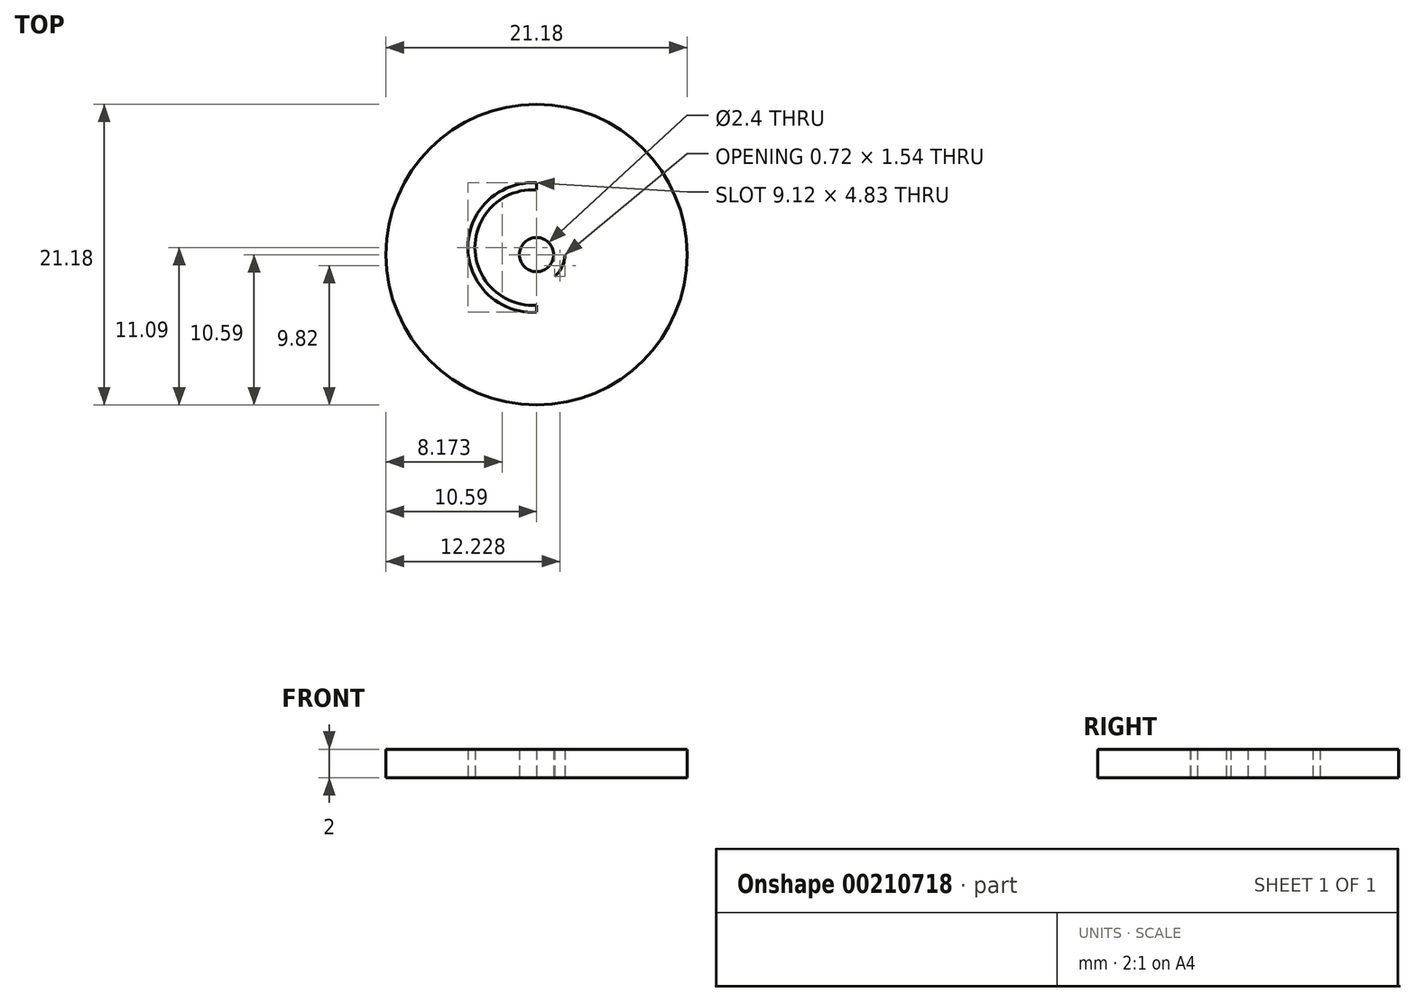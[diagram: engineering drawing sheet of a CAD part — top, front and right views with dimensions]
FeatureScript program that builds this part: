
annotation { "Feature Type Name" : "Feature", "Feature Type Description" : "" }
export const myFeature = defineFeature(function(context is Context, id is Id, definition is map)
    precondition{}
    {
        {
            var Q0;
            Q0=qCreatedBy(makeId("Top.planeOp"),FACE);
            var sketch = newSketch(context, id + "F0", { "sketchPlane" : qUnion([Q0])});
            skPoint(sketch, "E0", {"position": v(-1.84, 3.56) * mm});
            skArc(sketch, "E1", {"start": v(0, -3.56) * mm, "mid": v(3.33, 0) * mm, "end": v(0, 3.56) * mm});
            skArc(sketch, "E2", {"start": v(0, 3.56) * mm, "mid": v(-3.27, 0.5) * mm, "end": v(0, -2.56) * mm});
            skArc(sketch, "E3", {"start": v(0, -2.56) * mm, "mid": v(2.4, 0) * mm, "end": v(0, 2.56) * mm});
            skArc(sketch, "E4", {"start": v(0, 2.56) * mm, "mid": v(-2.2, 0.5) * mm, "end": v(0, -1.56) * mm});
            skPoint(sketch, "E5.end.orphan", {"position": v(-0.75, 4.56) * mm});
            skPoint(sketch, "E6.orphan", {"position": v(4, -0.14) * mm});
            skPoint(sketch, "E7.center.orphan", {"position": v(0, 0) * mm});
            skArc(sketch, "E8", {"start": v(0, -3.56) * mm, "mid": v(-4.33, 0.5) * mm, "end": v(0, 4.56) * mm});
            skLineSegment(sketch, "E9", {"start": v(0, 2.56) * mm, "end": v(0, 3.06) * mm});
            skLineSegment(sketch, "E10", {"start": v(0, -2.56) * mm, "end": v(0, -3.06) * mm});
            skLineSegment(sketch, "E11", {"start": v(0, 3.56) * mm, "end": v(0, 4.06) * mm});
            skLineSegment(sketch, "E12", {"start": v(0, -3.56) * mm, "end": v(0, -4.06) * mm});
            skLineSegment(sketch, "E13", {"start": v(0, 4.56) * mm, "end": v(0, 5.06) * mm});
            skArc(sketch, "E14", {"start": v(0, 3.06) * mm, "mid": v(-2.7, 0.5) * mm, "end": v(0, -2.06) * mm});
            skPoint(sketch, "E15", {"position": v(-2.2, 0.66) * mm});
            skPoint(sketch, "E16", {"position": v(-2.68, 0.78) * mm});
            skArc(sketch, "E17", {"start": v(0, -3.06) * mm, "mid": v(2.9, 0) * mm, "end": v(0, 3.06) * mm});
            skPoint(sketch, "E18", {"position": v(2.4, 0) * mm});
            skPoint(sketch, "E19", {"position": v(2.9, 0) * mm});
            skPoint(sketch, "E19.positionSnap0", {"position": v(2.9, 0) * mm});
            skArc(sketch, "E20", {"start": v(0, 4.06) * mm, "mid": v(-3.77, 0.5) * mm, "end": v(0, -3.06) * mm});
            skPoint(sketch, "E21", {"position": v(-3.77, 0.5) * mm});
            skPoint(sketch, "E22", {"position": v(-3.27, 0.5) * mm});
            skArc(sketch, "E23", {"start": v(0, -4.06) * mm, "mid": v(3.83, 0) * mm, "end": v(0, 4.06) * mm});
            skPoint(sketch, "E24", {"position": v(3.33, 0) * mm});
            skPoint(sketch, "E25", {"position": v(3.83, 0) * mm});
            skPoint(sketch, "E25.positionSnap0", {"position": v(3.83, 0) * mm});
            skArc(sketch, "E26", {"start": v(0, 5.06) * mm, "mid": v(-4.83, 0.5) * mm, "end": v(0, -4.06) * mm});
            skPoint(sketch, "E27", {"position": v(-4.33, 0.5) * mm});
            skPoint(sketch, "E28", {"position": v(-4.83, 0.5) * mm});
            skPoint(sketch, "E29", {"position": v(0, -4.56) * mm});
            skLineSegment(sketch, "E30", {"start": v(0, -4.56) * mm, "end": v(0, -5.06) * mm});
            skPoint(sketch, "E31", {"position": v(0, -5.56) * mm});
            skLineSegment(sketch, "E32", {"start": v(0, -5.56) * mm, "end": v(0, -6.06) * mm});
            skPoint(sketch, "E33", {"position": v(0, -6.56) * mm});
            skLineSegment(sketch, "E34", {"start": v(0, -6.56) * mm, "end": v(0, -7.06) * mm});
            skLineSegment(sketch, "E35", {"start": v(4.33, 0) * mm, "end": v(4.83, 0) * mm});
            skLineSegment(sketch, "E36", {"start": v(5.33, 0) * mm, "end": v(5.83, 0) * mm});
            skLineSegment(sketch, "E37", {"start": v(6.33, 0) * mm, "end": v(6.88, 0) * mm});
            skArc(sketch, "E38", {"start": v(0, -4.56) * mm, "mid": v(3.07, -3.14) * mm, "end": v(4.33, 0) * mm});
            skArc(sketch, "E39", {"start": v(0, -5.06) * mm, "mid": v(3.43, -3.5) * mm, "end": v(4.83, 0) * mm});
            skArc(sketch, "E40", {"start": v(4.33, 0) * mm, "mid": v(3.07, 3.14) * mm, "end": v(0, 4.56) * mm});
            skPoint(sketch, "E41", {"position": v(-2.7, 0.5) * mm});
            skPoint(sketch, "E42", {"position": v(-2.2, 0.5) * mm});
            skPoint(sketch, "E42.positionSnap0", {"position": v(-2.2, 0.5) * mm});
            skArc(sketch, "E43", {"start": v(4.83, 0) * mm, "mid": v(3.43, 3.5) * mm, "end": v(0, 5.06) * mm});
            skLineSegment(sketch, "E44", {"start": v(0, 5.56) * mm, "end": v(0, 6.06) * mm});
            skLineSegment(sketch, "E45", {"start": v(0, 6.56) * mm, "end": v(0, 7.06) * mm});
            skLineSegment(sketch, "E46", {"start": v(0, 7.56) * mm, "end": v(0, 8.06) * mm});
            skArc(sketch, "E47", {"start": v(5.33, 0) * mm, "mid": v(3.83, 3.9) * mm, "end": v(0, 5.56) * mm});
            skArc(sketch, "E48", {"start": v(0, 5.56) * mm, "mid": v(-5.33, 0.5) * mm, "end": v(0, -4.56) * mm});
            skArc(sketch, "E49", {"start": v(0, 6.06) * mm, "mid": v(-5.83, 0.5) * mm, "end": v(0, -5.06) * mm});
            skArc(sketch, "E50", {"start": v(0, -5.56) * mm, "mid": v(3.78, -3.85) * mm, "end": v(5.33, 0) * mm});
            skArc(sketch, "E51", {"start": v(0, -6.06) * mm, "mid": v(5.83, 0) * mm, "end": v(0, 6.06) * mm});
            skArc(sketch, "E52", {"start": v(0, 6.56) * mm, "mid": v(-6.3, 0.5) * mm, "end": v(0, -5.56) * mm});
            skArc(sketch, "E53", {"start": v(0, 7.06) * mm, "mid": v(-6.8, 0.5) * mm, "end": v(0, -6.06) * mm});
            skPoint(sketch, "E54", {"position": v(-6.8, 0.5) * mm});
            skPoint(sketch, "E55", {"position": v(-6.3, 0.5) * mm});
            skPoint(sketch, "E56", {"position": v(-5.83, 0.5) * mm});
            skPoint(sketch, "E57", {"position": v(-5.33, 0.5) * mm});
            skArc(sketch, "E58", {"start": v(0, -6.56) * mm, "mid": v(6.33, 0) * mm, "end": v(0, 6.56) * mm});
            skArc(sketch, "E59", {"start": v(0, -7.06) * mm, "mid": v(6.88, 0) * mm, "end": v(0, 7.06) * mm});
            skArc(sketch, "E60", {"start": v(0, 7.56) * mm, "mid": v(-7.3, 0.5) * mm, "end": v(0, -6.56) * mm});
            skArc(sketch, "E61", {"start": v(0, 8.06) * mm, "mid": v(-7.8, 0.5) * mm, "end": v(0, -7.06) * mm});
            skArc(sketch, "E62", {"start": v(1.28, -1.54) * mm, "mid": v(0.61, 1.9) * mm, "end": v(-1.93, -0.5) * mm});
            skLineSegment(sketch, "E63", {"start": v(0, 0) * mm, "end": v(1.67, -1.1) * mm});
            skArc(sketch, "E64", {"start": v(0, -2.06) * mm, "mid": v(1.4, -1.42) * mm, "end": v(2, 0) * mm});
            skCircle(sketch, "E65", {"center": v(0, 0) * mm, "radius": 1.2 * mm});
            skPoint(sketch, "E66", {"position": v(1, -0.67) * mm});
            skPoint(sketch, "E67", {"position": v(-1.93, -0.5) * mm});
            skCircle(sketch, "E68", {"center": v(0, 0) * mm, "radius": 8.6 * mm});
            skCircle(sketch, "E69", {"center": v(0, 0) * mm, "radius": 10.6 * mm});
            skArc(sketch, "E70", {"start": v(0, 8.06) * mm, "mid": v(0.58, 8.13) * mm, "end": v(1, 8.54) * mm});
            skArc(sketch, "E71", {"start": v(0, 7.56) * mm, "mid": v(1.07, 7.74) * mm, "end": v(1.94, 8.37) * mm});
            skSolve(sketch);
        }
        {
            var Q0;
            Q0=makeQuery(id+"F0.imprint","IMPRINT",FACE,{"disambiguationData":[TD([[makeQuery(id+"F0.imprint","IMPRINT",EDGE,{"derivedFrom":sQuery(id+"F0.wireOp",EDGE,"E69")}),1.0]])]});
            var Q1;
            Q1=makeQuery(id+"F0.imprint","IMPRINT",FACE,{"disambiguationData":[TD([[makeQuery(id+"F0.imprint","IMPRINT",EDGE,{"derivedFrom":sQuery(id+"F0.wireOp",EDGE,"E46")}),-1.0]])]});
            var Q2;
            Q2=makeQuery(id+"F0.imprint","IMPRINT",FACE,{"disambiguationData":[TD([[makeQuery(id+"F0.imprint","IMPRINT",EDGE,{"derivedFrom":sQuery(id+"F0.wireOp",EDGE,"E34")}),-1.0]])]});
            var Q3;
            {var subQ7=sQuery(id+"F0.wireOp",EDGE,"E9");Q3=makeQuery(id+"F0.imprint","IMPRINT",FACE,{"disambiguationData":[TD([[makeQuery(id+"F0.imprint","IMPRINT",EDGE,{"derivedFrom":subQ7}),1.0]])]});}
            var Q4;
            Q4=makeQuery(id+"F0.imprint","IMPRINT",FACE,{"disambiguationData":[TD([[makeQuery(id+"F0.imprint","IMPRINT",EDGE,{"derivedFrom":sQuery(id+"F0.wireOp",EDGE,"E3")}),-1.0]])]});
            var Q5;
            Q5=makeQuery(id+"F0.imprint","IMPRINT",FACE,{"disambiguationData":[TD([[makeQuery(id+"F0.imprint","IMPRINT",EDGE,{"derivedFrom":sQuery(id+"F0.wireOp",EDGE,"E1")}),-1.0]])]});
            var Q6;
            Q6=makeQuery(id+"F0.imprint","IMPRINT",FACE,{"disambiguationData":[TD([[makeQuery(id+"F0.imprint","IMPRINT",EDGE,{"derivedFrom":sQuery(id+"F0.wireOp",EDGE,"E8")}),1.0]])]});
            var Q7;
            Q7=makeQuery(id+"F0.imprint","IMPRINT",FACE,{"disambiguationData":[TD([[makeQuery(id+"F0.imprint","IMPRINT",EDGE,{"derivedFrom":sQuery(id+"F0.wireOp",EDGE,"E2")}),-1.0]])]});
            var Q8;
            Q8=makeQuery(id+"F0.imprint","IMPRINT",FACE,{"disambiguationData":[TD([[makeQuery(id+"F0.imprint","IMPRINT",EDGE,{"derivedFrom":sQuery(id+"F0.wireOp",EDGE,"E13")}),-1.0]])]});
            var Q9;
            Q9=makeQuery(id+"F0.imprint","IMPRINT",FACE,{"disambiguationData":[TD([[makeQuery(id+"F0.imprint","IMPRINT",EDGE,{"derivedFrom":sQuery(id+"F0.wireOp",EDGE,"E30")}),1.0]])]});
            var Q10;
            Q10=makeQuery(id+"F0.imprint","IMPRINT",FACE,{"disambiguationData":[TD([[makeQuery(id+"F0.imprint","IMPRINT",EDGE,{"derivedFrom":sQuery(id+"F0.wireOp",EDGE,"E30")}),-1.0]])]});
            var Q11;
            {var subQ0=sQuery(id+"F0.wireOp",EDGE,"E36");Q11=makeQuery(id+"F0.imprint","IMPRINT",FACE,{"disambiguationData":[TD([[makeQuery(id+"F0.imprint","IMPRINT",EDGE,{"derivedFrom":subQ0}),1.0]])]});}
            var Q12;
            {var subQ0=sQuery(id+"F0.wireOp",EDGE,"E32");Q12=makeQuery(id+"F0.imprint","IMPRINT",FACE,{"disambiguationData":[TD([[makeQuery(id+"F0.imprint","IMPRINT",EDGE,{"derivedFrom":subQ0}),1.0]])]});}
            var Q13;
            Q13=makeQuery(id+"F0.imprint","IMPRINT",FACE,{"disambiguationData":[TD([[makeQuery(id+"F0.imprint","IMPRINT",EDGE,{"derivedFrom":sQuery(id+"F0.wireOp",EDGE,"E32")}),-1.0]])]});
            var Q14;
            {var subQ0=sQuery(id+"F0.wireOp",EDGE,"E37");Q14=makeQuery(id+"F0.imprint","IMPRINT",FACE,{"disambiguationData":[TD([[makeQuery(id+"F0.imprint","IMPRINT",EDGE,{"derivedFrom":subQ0}),1.0]])]});}
            var Q15;
            {var subQ0=sQuery(id+"F0.wireOp",EDGE,"E34");Q15=makeQuery(id+"F0.imprint","IMPRINT",FACE,{"disambiguationData":[TD([[makeQuery(id+"F0.imprint","IMPRINT",EDGE,{"derivedFrom":subQ0}),1.0]])]});}
            extrude(context, id + "F1", {"entities" : qUnion([Q0, Q1, Q2, Q3, Q4, Q5, Q6, Q7, Q8, Q9, Q10, Q11, Q12, Q13, Q14, Q15]), "depth" : 2 * mm});
        }
    });
